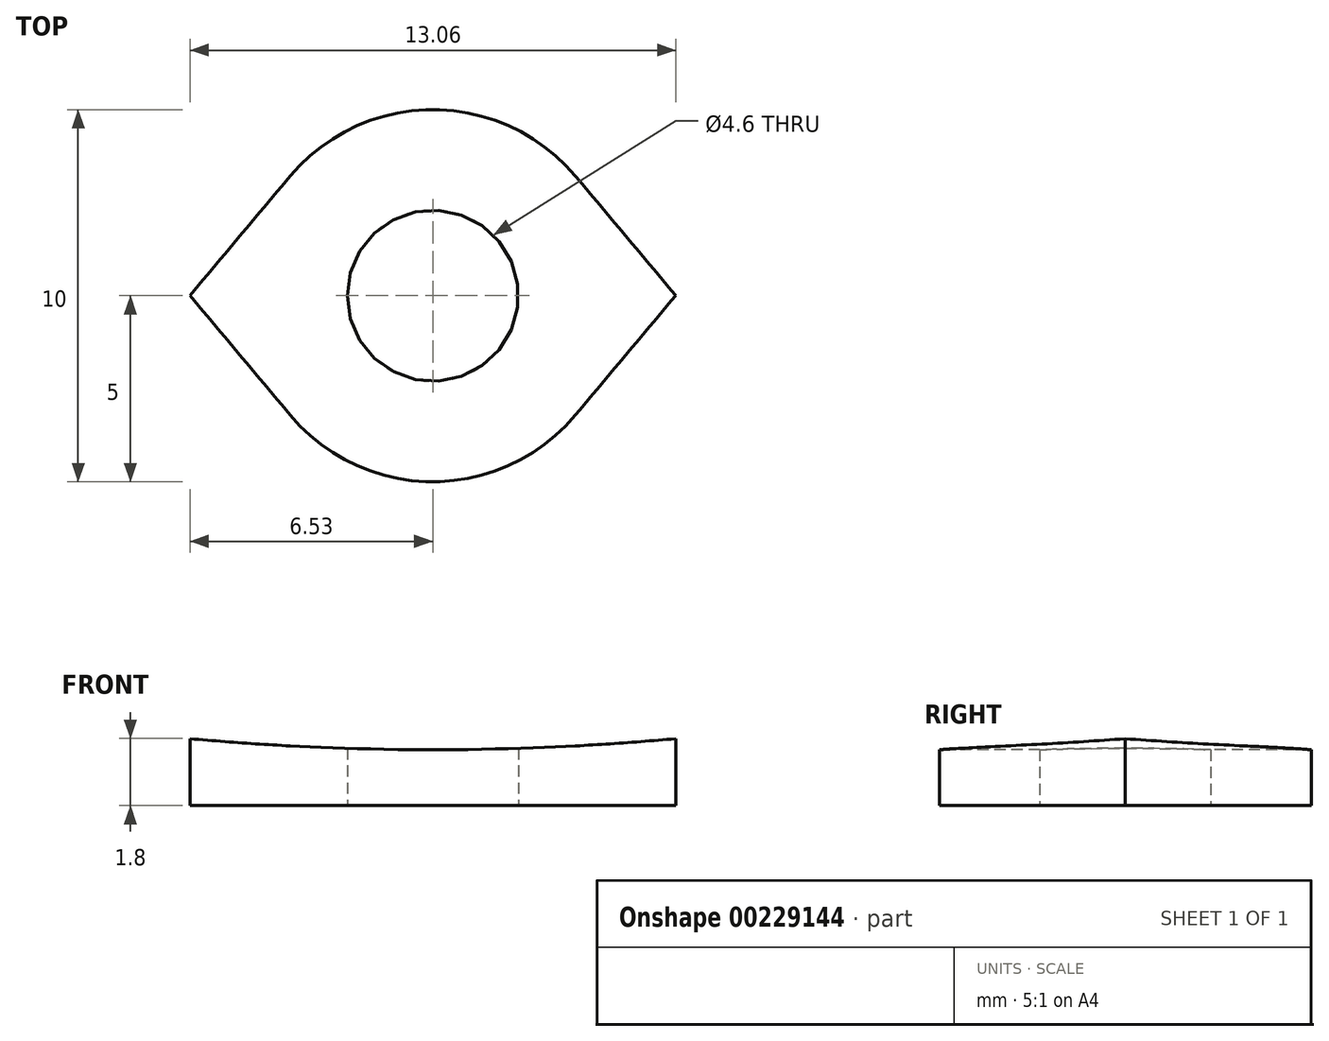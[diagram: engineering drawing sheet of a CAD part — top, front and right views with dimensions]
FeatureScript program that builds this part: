
annotation { "Feature Type Name" : "Feature", "Feature Type Description" : "" }
export const myFeature = defineFeature(function(context is Context, id is Id, definition is map)
    precondition{}
    {
        {
            var Q0;
            Q0=qCreatedBy(makeId("Top.planeOp"),FACE);
            var sketch = newSketch(context, id + "F0", { "sketchPlane" : qUnion([Q0])});
            skArc(sketch, "E0", {"start": v(-3.83, -3.21) * mm, "mid": v(0, -5) * mm, "end": v(3.83, -3.21) * mm});
            skCircle(sketch, "E1", {"center": v(0, 0) * mm, "radius": 2.3 * mm});
            skLineSegment(sketch, "E2", {"start": v(-6.53, 0) * mm, "end": v(-3.83, -3.21) * mm});
            skPoint(sketch, "E3.start.orphan", {"position": v(-5, 0) * mm});
            skLineSegment(sketch, "E4.MirrorCS", {"start": v(-6.53, 0) * mm, "end": v(-3.83, 3.21) * mm});
            skLineSegment(sketch, "E5.MirrorCS", {"start": v(6.53, 0) * mm, "end": v(3.83, -3.21) * mm});
            skLineSegment(sketch, "E6.MirrorCS", {"start": v(6.53, 0) * mm, "end": v(3.83, 3.21) * mm});
            skArc(sketch, "E7.trimOffspring", {"start": v(3.83, 3.21) * mm, "mid": v(0, 5) * mm, "end": v(-3.83, 3.21) * mm});
            skSolve(sketch);
        }
        {
            var Q0;
            Q0 = qSketchRegion(id + "F0", true);
            extrude(context, id + "F1", {"entities" : qUnion([Q0]), "depth" : 3 * mm});
        }
        {
            var Q0;
            Q0=qCreatedBy(makeId("Front.planeOp"),FACE);
            var sketch = newSketch(context, id + "F2", { "sketchPlane" : qUnion([Q0])});
            skCircle(sketch, "E8", {"center": v(0, 73.7) * mm, "radius": 72.2 * mm});
            skSolve(sketch);
        }
        {
            var Q0;
            Q0 = qSketchRegion(id + "F2", true);
            extrude(context, id + "F3", {"entities" : qUnion([Q0]), "operationType" : NewBodyOperationType.REMOVE, "oppositeDirection" : true, "depth" : 25 * mm, "hasSecondDirection" : true, "secondDirectionOppositeDirection" : false, "secondDirectionDepth" : 25 * mm});
        }
    });
